# Revit family: 8114956233(2020)
name_source: partatom
category: Plumbing Fixtures
revit_build: Autodesk Revit 2018 (Build: 20170223_1515(x64)
units: mm (PartAtom-declared; Revit-internal decimal feet)

## family parameters
Always vertical = Yes
Cut with Voids When Loaded = No
OmniClass Number = 23.45.55.00
OmniClass Title = Sanitary Faucets, Wastes
Part Type = Normal
Room Calculation Point = No
Round Connector Dimension = Use Diameter
Shared = No
Work Plane-Based = No

## types (1)
- 8114956233 Cover part for bath and shower faucet
    2D/3D/BIM Files URL = http://static.hansa.com
    3D View = https://static.hansa.com
    Advanced Features = Inner body made of DZR brass;Manual, ceramic, pressure independent diverter with volume control and stop function for two outlets
    Ambience photo = http://static.hansa.com
    Approval ABP = PA-IX 38188/IDD
    Approval SVGW = 1805-6755
    AssetType = Fixed
    BIMObjectName = 8114956233(2020)
    Backflow Prevention EN1717 = EB
    BodyMaterial = Brass
    Brand = HANSA
    Catalog Drawing URL = http://static.hansa.com
    Category = Bathroom;Shower
    CloseOffRating = 0
    Color = Chrome
    Concealed Parts = Square rosette;Fastening of the function unit with screws;BLUECLICK for an easy, screwless trim plate installation;BLUETUNE alignment after installation of +/- 3,5º
    Dimension Drawing URL = http://static.hansa.com
    Diverter = Turn operated diverter
    DurationUnit = Year
    EAN Number = 4057304015847
    EN Standard = EN 1111
    ETIM Class Number = EC010546 Mechanical control system for shower
    FDV Document URL = http://www.hansa.com
    FaucetMainMaterial = Brass
    Features = Trim Kit;Thermostatic
    Finish = Polished
    Flow Drawing URL = http://static.hansa.com
    Flow Rate At 300kPa = 340.3 L/s
    FlowCoefficient = 0
    Group = Bath and shower faucet
    IfcExportAs = IfcValveType
    IfcExportType = FAUCET
    Installation Type = Concealed wall mounting
    Installation and Maintenance Guide URL = http://static.hansa.com
    Interactive AR View URL = https://static.hansa.com
    Lever Handle = Temperature control handle;Flow control handle
    Manufacturer = HANSA
    ManufacturerName = HANSA
    ManufacturerURL = http://www.hansa.com
    Market = International;Germany;Austria;Belgium;Netherlands
    Material = Brass
    Max. Hot Water Supply = 80 °C
    Mechanical Parts = Thermostatic cartridge for automatic temperature control;Non-return valve(s)
    Mobile Product Information URL = http://mpi.hansa.com
    Model = 8114956233 Cover part for bath and shower faucet
    ModelReference = 8114956233
    NBSDescription = Water supply fittings for baths
    NBSReference = 45-35-70/315
    Name = 8114956233 Cover part for bath and shower faucet
    Name_en = 8114956233 Cover part for bath and shower faucet
    Noise Class = I (ISO 3822)
    NominalDepth = 79 mm
    NominalHeight = 150 mm
    NominalWidth = 150 mm
    Product Code = 8114956233
    Product Family = HANSALIVING
    Product Image URL = http://static.hansa.com
    Product URL = http://static.hansa.com
    Revision = 1
    Sales Package dimensions (LxWxH) = 204 x 186 x 174
    Shape = Sculptured
    Size = 150x80x150 mm
    Spare-Part Information URL = http://static.hansa.com
    Surface treatment = Matt black
    Technical DataSheet URL = http://www.hansa.com
    Temperature Adjustments = Safety stop against scalding at 38°C
    UNSPSC Class Number = 30181810 Faucet trim
    URL ABP = http://static.hansa.com
    URL Declaration of Conformity = http://static.hansa.com
    URL REACH = http://static.hansa.com
    URL SVGW = http://static.hansa.com
    Uniclass2 = Pr_40_30_96_10
    Uniclass2015Description = Bath thermostatic water supply sets
    Uniclass2015Reference = Pr_40_20_87_10
    Version = 2
    VersionDate = 01/07/2022
    Warranty Information URL = http://warranty.hansa.com
    WarrantyDescription = http://warranty.hansa.com
    WarrantyDurationUnit = Year
    Working Pressure = 100 - 1000 kPa
    WorkingPressure = 100 - 1000 kPa

## geometry (parser evidence)
native form markers: Sweep x4
no freeform markers — native parametric forms only
